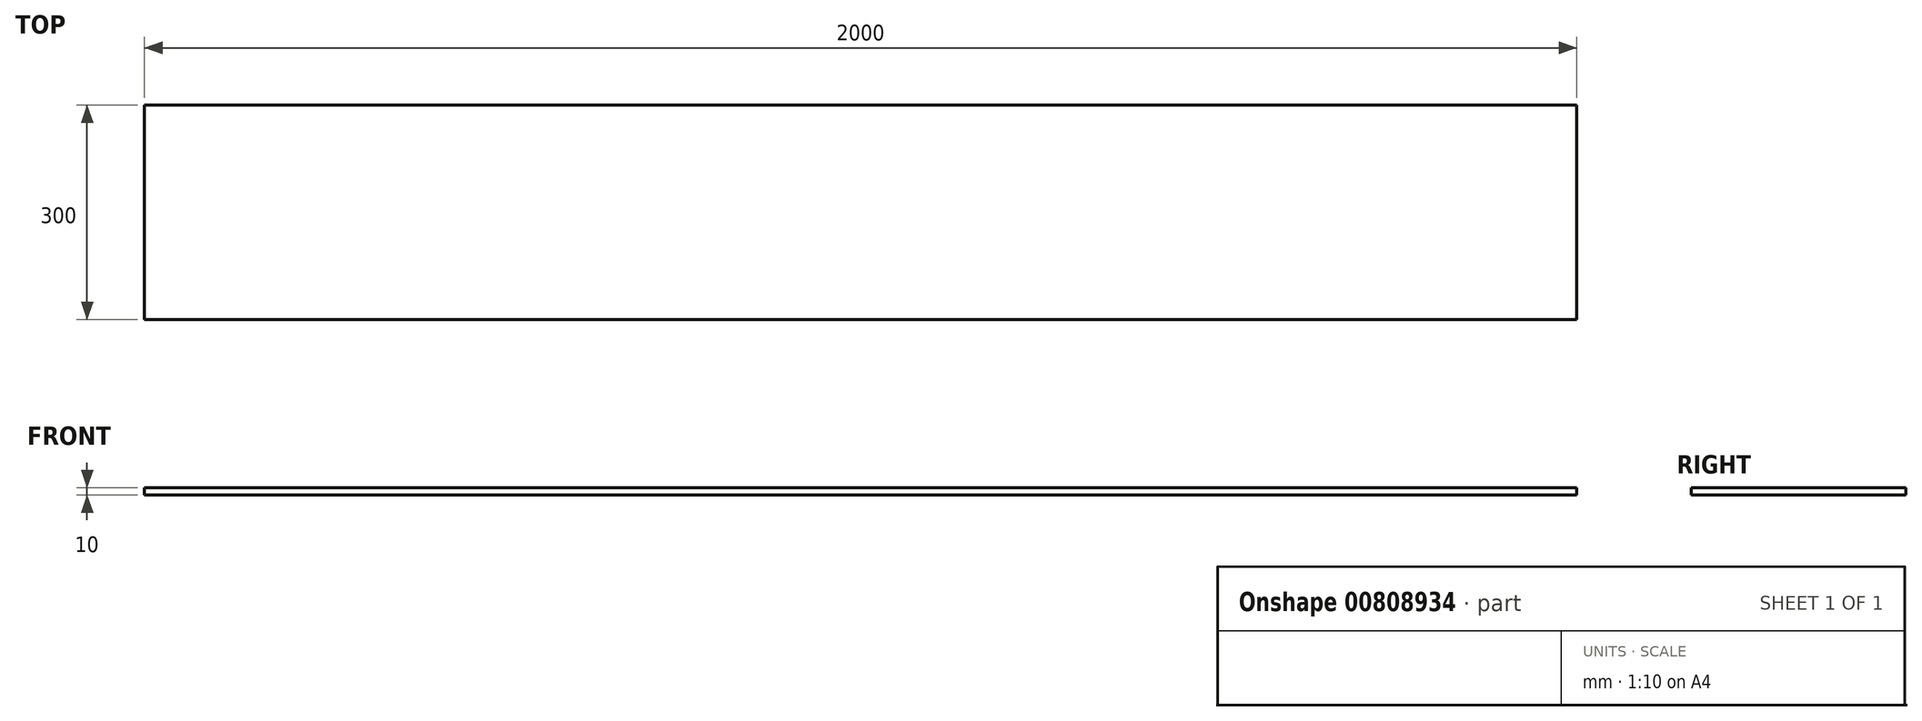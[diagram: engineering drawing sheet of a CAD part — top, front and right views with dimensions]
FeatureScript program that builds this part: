
annotation { "Feature Type Name" : "Feature", "Feature Type Description" : "" }
export const myFeature = defineFeature(function(context is Context, id is Id, definition is map)
    precondition{}
    {
        {
            var Q0;
            Q0=qCreatedBy(makeId("Top.planeOp"),FACE);
            var sketch = newSketch(context, id + "F0", { "sketchPlane" : qUnion([Q0])});
            skLineSegment(sketch, "E0.bottom", {"start": v(613.27, 926.22) * mm, "end": v(2613.27, 926.22) * mm});
            skLineSegment(sketch, "E0.top", {"start": v(613.27, 626.22) * mm, "end": v(2613.27, 626.22) * mm});
            skLineSegment(sketch, "E0.left", {"start": v(613.27, 926.22) * mm, "end": v(613.27, 626.22) * mm});
            skLineSegment(sketch, "E0.right", {"start": v(2613.27, 926.22) * mm, "end": v(2613.27, 626.22) * mm});
            skSolve(sketch);
        }
        {
            var Q0;
            Q0 = qSketchRegion(id + "F0", true);
            extrude(context, id + "F1", {"entities" : qUnion([Q0]), "depth" : 10 * mm, "offsetDistance" : 25 * mm});
        }
    });
